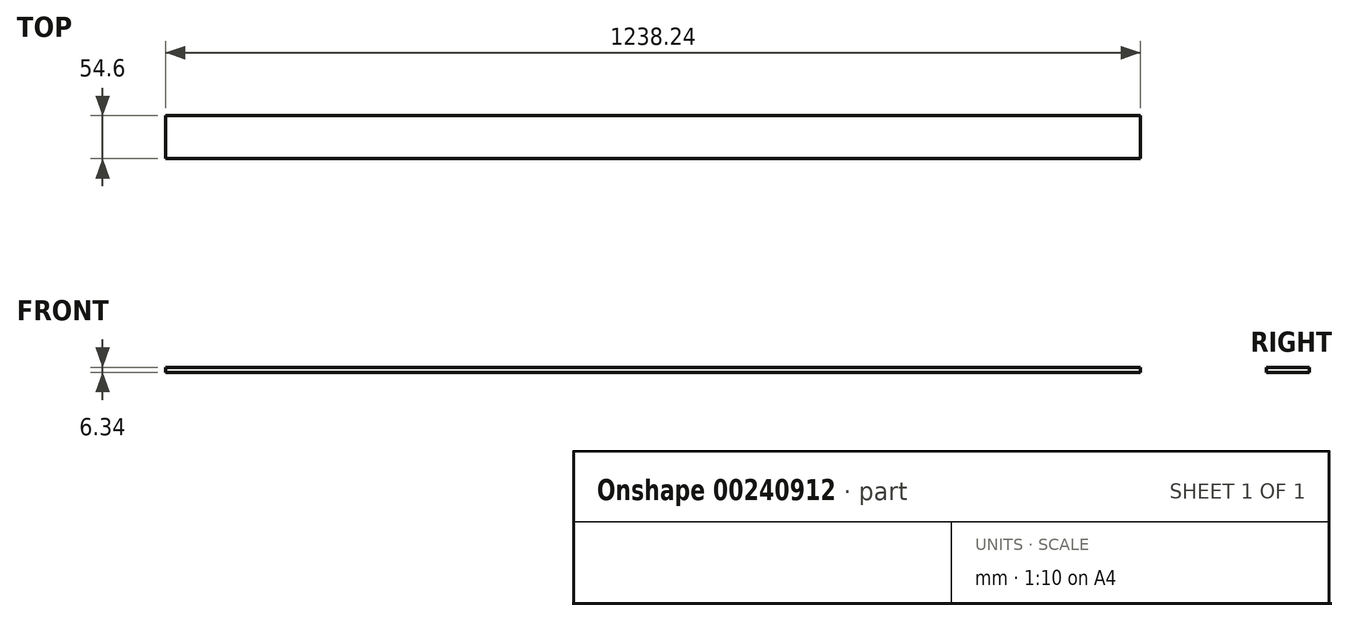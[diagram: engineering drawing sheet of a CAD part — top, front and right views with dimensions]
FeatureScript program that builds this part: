
annotation { "Feature Type Name" : "Feature", "Feature Type Description" : "" }
export const myFeature = defineFeature(function(context is Context, id is Id, definition is map)
    precondition{}
    {
        {
            var Q0;
            Q0=qCreatedBy(makeId("Right.planeOp"),FACE);
            var sketch = newSketch(context, id + "F0", { "sketchPlane" : qUnion([Q0])});
            skLineSegment(sketch, "E0.bottom", {"start": v(27.3, -3.18) * mm, "end": v(-27.3, -3.18) * mm});
            skLineSegment(sketch, "E0.top", {"start": v(27.3, 3.18) * mm, "end": v(-27.3, 3.17) * mm});
            skLineSegment(sketch, "E0.left", {"start": v(27.3, -3.18) * mm, "end": v(27.3, 3.18) * mm});
            skLineSegment(sketch, "E0.right", {"start": v(-27.3, -3.18) * mm, "end": v(-27.3, 3.17) * mm});
            skPoint(sketch, "E0.middle", {"position": v(0, 0) * mm});
            skSolve(sketch);
        }
        {
            var Q0;
            Q0=qSketchRegion(id+"F0",true);
            extrude(context, id + "F1", {"entities" : qUnion([Q0]), "depth" : 619.12 * mm, "hasSecondDirection" : true, "secondDirectionOppositeDirection" : true, "secondDirectionDepth" : 619.12 * mm});
        }
    });
